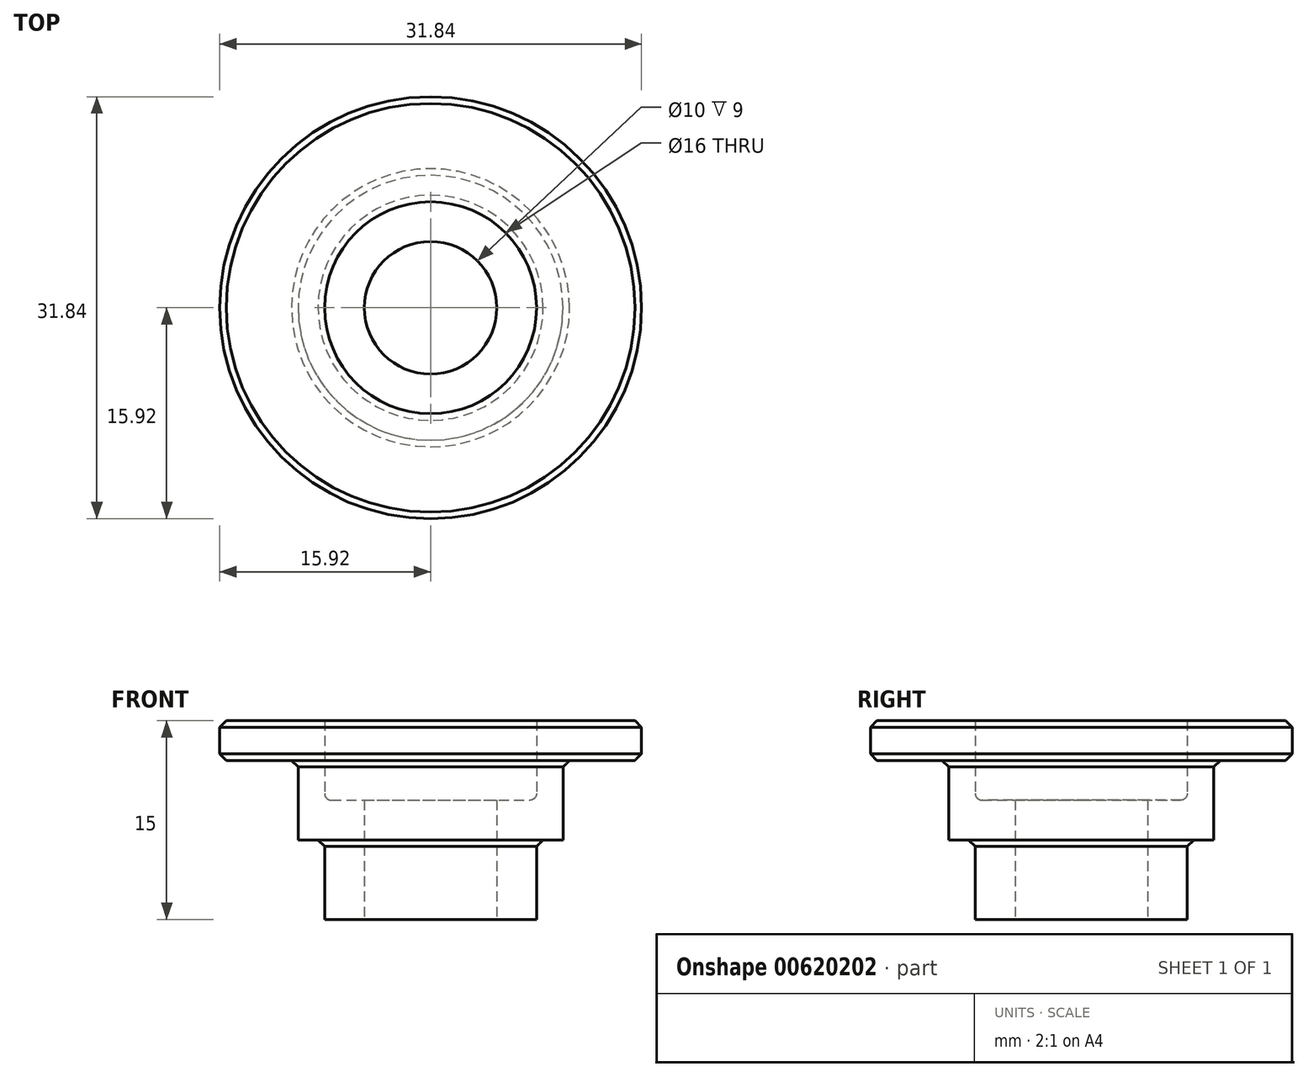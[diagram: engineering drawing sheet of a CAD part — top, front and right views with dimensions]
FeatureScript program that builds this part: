
annotation { "Feature Type Name" : "Feature", "Feature Type Description" : "" }
export const myFeature = defineFeature(function(context is Context, id is Id, definition is map)
    precondition{}
    {
        {
            var Q0;
            Q0=qCreatedBy(makeId("Front.planeOp"),FACE);
            var sketch = newSketch(context, id + "F0", { "sketchPlane" : qUnion([Q0])});
            skLineSegment(sketch, "E0", {"start": v(0, 0) * mm, "end": v(0, 16.14) * mm, "construction": true});
            skLineSegment(sketch, "E1", {"start": v(-5, 0) * mm, "end": v(-5, 15) * mm, "construction": true});
            skLineSegment(sketch, "E2", {"start": v(-5, 15) * mm, "end": v(-15.92, 15) * mm, "construction": true});
            skLineSegment(sketch, "E3", {"start": v(-10, 12) * mm, "end": v(-10, 6) * mm});
            skLineSegment(sketch, "E4", {"start": v(-10, 6) * mm, "end": v(-8, 6) * mm});
            skLineSegment(sketch, "E5", {"start": v(-8, 6) * mm, "end": v(-8, 0) * mm});
            skLineSegment(sketch, "E6", {"start": v(-8, 0) * mm, "end": v(-5, 0) * mm});
            skLineSegment(sketch, "E7", {"start": v(-8, 15) * mm, "end": v(-8, 9.5) * mm});
            skLineSegment(sketch, "E8", {"start": v(-7.5, 9) * mm, "end": v(-5, 9) * mm});
            skLineSegment(sketch, "E9", {"start": v(-5, 9) * mm, "end": v(-5, 0) * mm, "construction": true});
            skPoint(sketch, "E10.visualSharp", {"position": v(-8, 9) * mm});
            skArc(sketch, "E10.filletArc", {"start": v(-8, 9.5) * mm, "mid": v(-7.85, 9.15) * mm, "end": v(-7.5, 9) * mm});
            skLineSegment(sketch, "E11", {"start": v(-5, 9) * mm, "end": v(-5, 0) * mm});
            skLineSegment(sketch, "E12", {"start": v(-15.92, 15) * mm, "end": v(-15.92, 12) * mm});
            skLineSegment(sketch, "E13", {"start": v(-15.92, 12) * mm, "end": v(-10, 12) * mm});
            skLineSegment(sketch, "E14", {"start": v(-8, 15) * mm, "end": v(-15.92, 15) * mm});
            skSolve(sketch);
        }
        {
            var Q0;
            Q0 = qSketchRegion(id + "F0", true);
            var Q1;
            Q1=sQuery(id+"F0.wireOp",EDGE,"E0");
            revolve(context, id + "F1", {"entities" : qUnion([Q0]), "axis" : qUnion([Q1]), "revolveType" : RevolveType.FULL});
        }
        {
            var Q0;
            Q0=makeQuery(id+"F1.opRevolve","SWEPT_EDGE",EDGE,{"disambiguationData":[OSD([sQuery(id+"F0.wireOp",EDGE,"E4"),sQuery(id+"F0.wireOp",EDGE,"E5")])]});
            chamfer(context, id + "F2", {"entities" : qUnion([Q0]), "width" : 0.5 * mm, "tangentPropagation" : true});
        }
        {
            var Q0;
            Q0=makeQuery(id+"F1.opRevolve","SWEPT_EDGE",EDGE,{"disambiguationData":[OSD([sQuery(id+"F0.wireOp",EDGE,"E12"),sQuery(id+"F0.wireOp",EDGE,"E13")])]});
            var Q1;
            Q1=makeQuery(id+"F1.opRevolve","SWEPT_EDGE",EDGE,{"disambiguationData":[OSD([sQuery(id+"F0.wireOp",EDGE,"E12"),sQuery(id+"F0.wireOp",EDGE,"E14")])]});
            var Q2;
            Q2=makeQuery(id+"F1.opRevolve","SWEPT_EDGE",EDGE,{"disambiguationData":[OSD([sQuery(id+"F0.wireOp",EDGE,"E3"),sQuery(id+"F0.wireOp",EDGE,"E13")])]});
            chamfer(context, id + "F3", {"entities" : qUnion([Q0, Q1, Q2]), "width" : 0.5 * mm, "tangentPropagation" : true});
        }
    });
